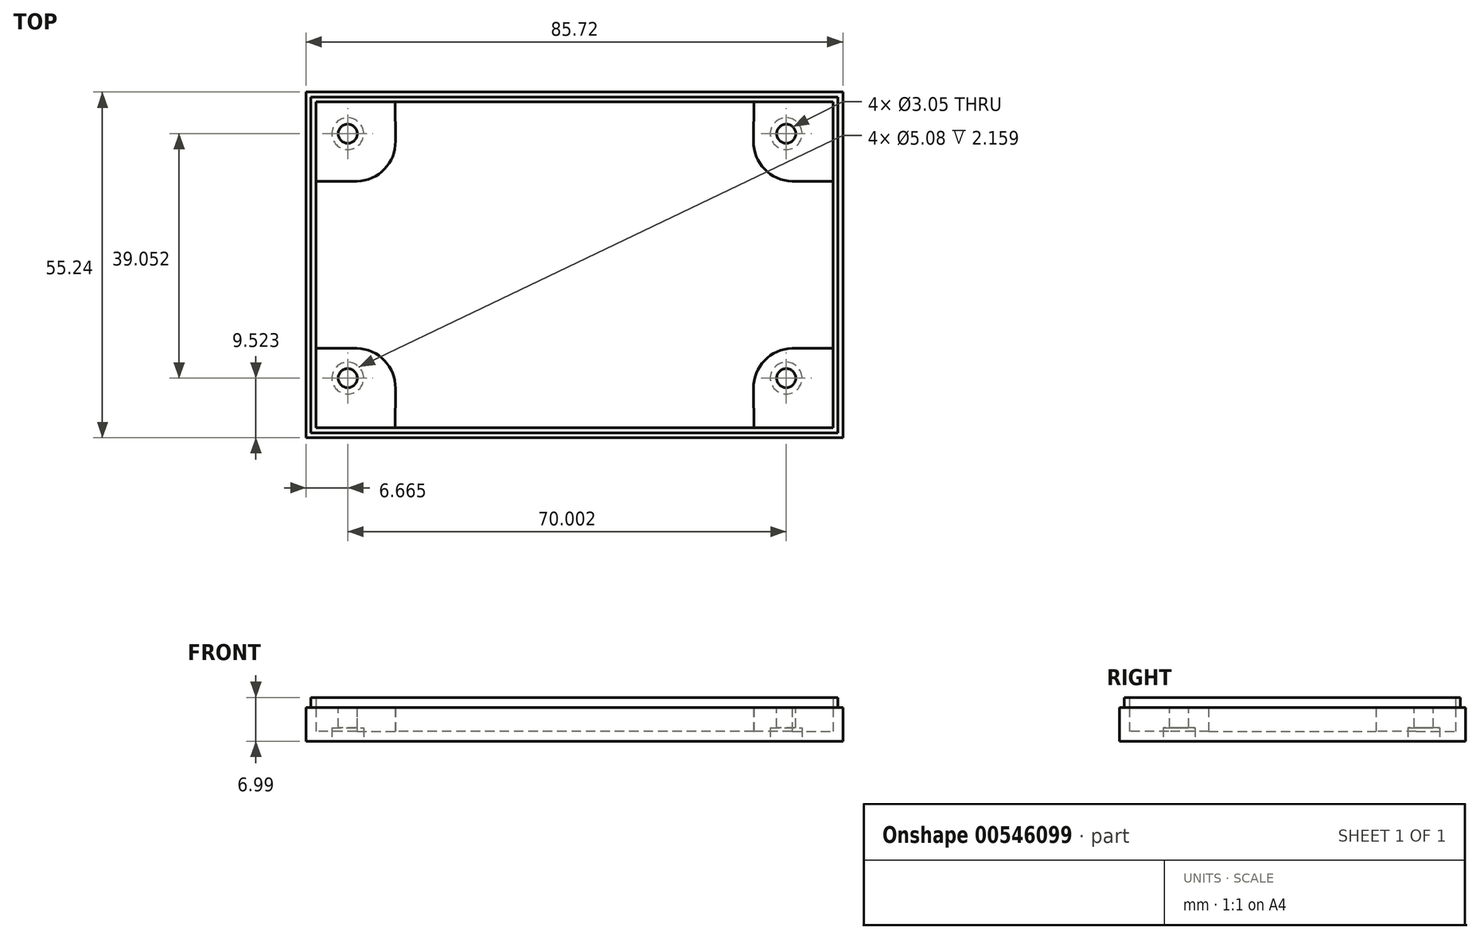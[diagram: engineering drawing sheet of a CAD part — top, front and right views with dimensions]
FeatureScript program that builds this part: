
annotation { "Feature Type Name" : "Feature", "Feature Type Description" : "" }
export const myFeature = defineFeature(function(context is Context, id is Id, definition is map)
    precondition{}
    {
        {
            var Q0;
            Q0=qCreatedBy(makeId("Top.planeOp"),FACE);
            var sketch = newSketch(context, id + "F0", { "sketchPlane" : qUnion([Q0])});
            skLineSegment(sketch, "E0.bottom", {"start": v(42.86, -27.62) * mm, "end": v(-42.86, -27.62) * mm});
            skLineSegment(sketch, "E0.top", {"start": v(42.86, 27.62) * mm, "end": v(-42.86, 27.62) * mm});
            skLineSegment(sketch, "E0.left", {"start": v(42.86, -27.62) * mm, "end": v(42.86, 27.62) * mm});
            skLineSegment(sketch, "E0.right", {"start": v(-42.86, -27.62) * mm, "end": v(-42.86, 27.62) * mm});
            skPoint(sketch, "E0.middle", {"position": v(0, 0) * mm});
            skSolve(sketch);
        }
        {
            var Q0;
            Q0=makeQuery(id+"F0.imprint","IMPRINT",FACE,{"disambiguationData":[TD([[makeQuery(id+"F0.imprint","IMPRINT",EDGE,{"derivedFrom":sQuery(id+"F0.wireOp",EDGE,"E0.bottom")}),-1.0]])]});
            extrude(context, id + "F1", {"entities" : qUnion([Q0]), "depth" : 7 * mm, "offsetDistance" : 25.4 * mm});
        }
        {
            var Q0;
            Q0=makeQuery(id+"F1.opExtrude","CAP_FACE",FACE,{"disambiguationData":[OSD([sQuery(id+"F0.wireOp",EDGE,"E0.bottom"),sQuery(id+"F0.wireOp",EDGE,"E0.top"),sQuery(id+"F0.wireOp",EDGE,"E0.left"),sQuery(id+"F0.wireOp",EDGE,"E0.right")])],"isStart":false});
            shell(context, id + "F2", {"entities" : qUnion([Q0]), "thickness" : 1.59 * mm});
        }
        {
            var Q0;
            Q0=makeQuery(id+"F2.opShell","OFFSET_FACE",FACE,{"disambiguationData":[OSD([sQuery(id+"F0.wireOp",EDGE,"E0.bottom"),sQuery(id+"F0.wireOp",EDGE,"E0.top"),sQuery(id+"F0.wireOp",EDGE,"E0.left"),sQuery(id+"F0.wireOp",EDGE,"E0.right")])]});
            var sketch = newSketch(context, id + "F3", { "sketchPlane" : qUnion([Q0])});
            skArc(sketch, "E1", {"start": v(-35.12, 13.34) * mm, "mid": v(-30.48, 15.15) * mm, "end": v(-28.58, 19.75) * mm});
            skLineSegment(sketch, "E2", {"start": v(-28.58, 19.75) * mm, "end": v(-28.64, 26.04) * mm});
            skLineSegment(sketch, "E3", {"start": v(-34.73, 13.34) * mm, "end": v(-41.28, 13.34) * mm});
            skLineSegment(sketch, "E4.MirrorCS", {"start": v(28.58, 19.75) * mm, "end": v(28.64, 26.04) * mm});
            skArc(sketch, "E5.MirrorCS", {"start": v(35.12, 13.34) * mm, "mid": v(30.48, 15.15) * mm, "end": v(28.58, 19.75) * mm});
            skLineSegment(sketch, "E6.MirrorCS", {"start": v(34.73, 13.34) * mm, "end": v(41.28, 13.34) * mm});
            skLineSegment(sketch, "E7.MirrorCS", {"start": v(-34.73, -13.34) * mm, "end": v(-41.28, -13.34) * mm});
            skArc(sketch, "E8.MirrorCS", {"start": v(-35.12, -13.34) * mm, "mid": v(-30.48, -15.15) * mm, "end": v(-28.58, -19.75) * mm});
            skLineSegment(sketch, "E9.MirrorCS", {"start": v(-28.58, -19.75) * mm, "end": v(-28.64, -26.04) * mm});
            skArc(sketch, "E10.MirrorCS", {"start": v(35.12, -13.34) * mm, "mid": v(30.48, -15.15) * mm, "end": v(28.58, -19.75) * mm});
            skLineSegment(sketch, "E11.MirrorCS", {"start": v(28.58, -19.75) * mm, "end": v(28.64, -26.04) * mm});
            skLineSegment(sketch, "E12.MirrorCS", {"start": v(34.73, -13.34) * mm, "end": v(41.28, -13.34) * mm});
            skSolve(sketch);
        }
        {
            var Q0;
            {var subQ7=sQuery(id+"F3.wireOp",EDGE,"E2");Q0=makeQuery(id+"F3.imprint","IMPRINT",FACE,{"disambiguationData":[TD([[makeQuery(id+"F3.imprint","IMPRINT",EDGE,{"derivedFrom":subQ7}),1.0]])]});}
            var Q1;
            {var subQ7=sQuery(id+"F3.wireOp",EDGE,"E4.MirrorCS");Q1=makeQuery(id+"F3.imprint","IMPRINT",FACE,{"disambiguationData":[TD([[makeQuery(id+"F3.imprint","IMPRINT",EDGE,{"derivedFrom":subQ7}),-1.0]])]});}
            var Q2;
            {var subQ7=sQuery(id+"F3.wireOp",EDGE,"E11.MirrorCS");Q2=makeQuery(id+"F3.imprint","IMPRINT",FACE,{"disambiguationData":[TD([[makeQuery(id+"F3.imprint","IMPRINT",EDGE,{"derivedFrom":subQ7}),1.0]])]});}
            var Q3;
            {var subQ0=sQuery(id+"F3.wireOp",EDGE,"E9.MirrorCS");Q3=makeQuery(id+"F3.imprint","IMPRINT",FACE,{"disambiguationData":[TD([[makeQuery(id+"F3.imprint","IMPRINT",EDGE,{"derivedFrom":subQ0}),-1.0]])]});}
            extrude(context, id + "F4", {"entities" : qUnion([Q0, Q1, Q2, Q3]), "operationType" : NewBodyOperationType.ADD, "depth" : 3.77 * mm, "offsetDistance" : 25.4 * mm});
        }
        {
            var Q0;
            Q0=makeQuery(id+"F4.opExtrude","CAP_FACE",FACE,{"disambiguationData":[OSD([sQuery(id+"F0.wireOp",EDGE,"E0.top"),sQuery(id+"F0.wireOp",EDGE,"E0.right"),sQuery(id+"F3.wireOp",EDGE,"E1"),sQuery(id+"F3.wireOp",EDGE,"E2"),sQuery(id+"F3.wireOp",EDGE,"E3")])],"isStart":false});
            var sketch = newSketch(context, id + "F5", { "sketchPlane" : qUnion([Q0])});
            skCircle(sketch, "E13", {"center": v(-36.2, 20.95) * mm, "radius": 1.52 * mm});
            skLineSegment(sketch, "E14.bottom", {"start": v(-36.2, 20.95) * mm, "end": v(33.8, 20.95) * mm, "construction": true});
            skLineSegment(sketch, "E14.top", {"start": v(-36.2, -18.1) * mm, "end": v(33.8, -18.1) * mm, "construction": true});
            skLineSegment(sketch, "E14.left", {"start": v(-36.2, 20.96) * mm, "end": v(-36.2, -18.1) * mm, "construction": true});
            skLineSegment(sketch, "E14.right", {"start": v(33.8, 20.96) * mm, "end": v(33.8, -18.1) * mm, "construction": true});
            skCircle(sketch, "E15", {"center": v(-36.2, -18.1) * mm, "radius": 1.52 * mm});
            skCircle(sketch, "E16", {"center": v(33.8, 20.95) * mm, "radius": 1.52 * mm});
            skCircle(sketch, "E17", {"center": v(33.8, -18.1) * mm, "radius": 1.52 * mm});
            skSolve(sketch);
        }
        {
            var Q0;
            Q0=makeQuery(id+"F5.imprint","IMPRINT",FACE,{"disambiguationData":[TD([[makeQuery(id+"F5.imprint","IMPRINT",EDGE,{"derivedFrom":sQuery(id+"F5.wireOp",EDGE,"E16")}),1.0]])]});
            var Q1;
            Q1=makeQuery(id+"F5.imprint","IMPRINT",FACE,{"disambiguationData":[TD([[makeQuery(id+"F5.imprint","IMPRINT",EDGE,{"derivedFrom":sQuery(id+"F5.wireOp",EDGE,"E13")}),1.0]])]});
            var Q2;
            Q2=makeQuery(id+"F5.imprint","IMPRINT",FACE,{"disambiguationData":[TD([[makeQuery(id+"F5.imprint","IMPRINT",EDGE,{"derivedFrom":sQuery(id+"F5.wireOp",EDGE,"E15")}),1.0]])]});
            var Q3;
            Q3=makeQuery(id+"F5.imprint","IMPRINT",FACE,{"disambiguationData":[TD([[makeQuery(id+"F5.imprint","IMPRINT",EDGE,{"derivedFrom":sQuery(id+"F5.wireOp",EDGE,"E17")}),1.0]])]});
            extrude(context, id + "F6", {"entities" : qUnion([Q0, Q1, Q2, Q3]), "operationType" : NewBodyOperationType.REMOVE, "endBound" : BoundingType.THROUGH_ALL, "oppositeDirection" : true, "depth" : 25.4 * mm, "offsetDistance" : 25.4 * mm});
        }
        {
            var Q0;
            Q0=makeQuery(id+"F1.opExtrude","CAP_FACE",FACE,{"disambiguationData":[OSD([sQuery(id+"F0.wireOp",EDGE,"E0.bottom"),sQuery(id+"F0.wireOp",EDGE,"E0.top"),sQuery(id+"F0.wireOp",EDGE,"E0.left"),sQuery(id+"F0.wireOp",EDGE,"E0.right")])],"isStart":true});
            var sketch = newSketch(context, id + "F7", { "sketchPlane" : qUnion([Q0])});
            skCircle(sketch, "E18", {"center": v(33.8, 18.1) * mm, "radius": 2.54 * mm});
            skCircle(sketch, "E19", {"center": v(33.8, -20.95) * mm, "radius": 2.54 * mm});
            skCircle(sketch, "E20", {"center": v(-36.2, -20.95) * mm, "radius": 2.54 * mm});
            skCircle(sketch, "E21", {"center": v(-36.2, 18.1) * mm, "radius": 2.54 * mm});
            skSolve(sketch);
        }
        {
            var Q0;
            Q0=makeQuery(id+"F7.imprint","IMPRINT",FACE,{"disambiguationData":[TD([[makeQuery(id+"F7.imprint","IMPRINT",EDGE,{"derivedFrom":sQuery(id+"F7.wireOp",EDGE,"E21")}),1.0]])]});
            var Q1;
            Q1=makeQuery(id+"F7.imprint","IMPRINT",FACE,{"disambiguationData":[TD([[makeQuery(id+"F7.imprint","IMPRINT",EDGE,{"derivedFrom":sQuery(id+"F7.wireOp",EDGE,"E18")}),1.0]])]});
            var Q2;
            Q2=makeQuery(id+"F7.imprint","IMPRINT",FACE,{"disambiguationData":[TD([[makeQuery(id+"F7.imprint","IMPRINT",EDGE,{"derivedFrom":sQuery(id+"F7.wireOp",EDGE,"E19")}),1.0]])]});
            var Q3;
            Q3=makeQuery(id+"F7.imprint","IMPRINT",FACE,{"disambiguationData":[TD([[makeQuery(id+"F7.imprint","IMPRINT",EDGE,{"derivedFrom":sQuery(id+"F7.wireOp",EDGE,"E20")}),1.0]])]});
            extrude(context, id + "F8", {"entities" : qUnion([Q0, Q1, Q2, Q3]), "operationType" : NewBodyOperationType.REMOVE, "oppositeDirection" : true, "depth" : 2.16 * mm, "offsetDistance" : 25.4 * mm});
        }
        {
            var Q0;
            Q0=makeQuery(id+"F1.opExtrude","CAP_FACE",FACE,{"disambiguationData":[OSD([sQuery(id+"F0.wireOp",EDGE,"E0.bottom"),sQuery(id+"F0.wireOp",EDGE,"E0.top"),sQuery(id+"F0.wireOp",EDGE,"E0.left"),sQuery(id+"F0.wireOp",EDGE,"E0.right")])],"isStart":false});
            var sketch = newSketch(context, id + "F9", { "sketchPlane" : qUnion([Q0])});
            skLineSegment(sketch, "E22", {"start": v(-42.86, -27.62) * mm, "end": v(-41.27, -26.04) * mm, "construction": true});
            skLineSegment(sketch, "E23", {"start": v(41.28, 26.04) * mm, "end": v(42.86, 27.62) * mm, "construction": true});
            skLineSegment(sketch, "E24.bottom", {"start": v(-42.07, -26.83) * mm, "end": v(42.07, -26.83) * mm});
            skLineSegment(sketch, "E24.top", {"start": v(-42.07, 26.83) * mm, "end": v(42.07, 26.83) * mm});
            skLineSegment(sketch, "E24.left", {"start": v(-42.07, -26.83) * mm, "end": v(-42.07, 26.83) * mm});
            skLineSegment(sketch, "E24.right", {"start": v(42.07, -26.83) * mm, "end": v(42.07, 26.83) * mm});
            skSolve(sketch);
        }
        {
            var Q0;
            Q0=makeQuery(id+"F9.imprint","IMPRINT",FACE,{"disambiguationData":[TD([[makeQuery(id+"F9.imprint","IMPRINT",EDGE,{"derivedFrom":sQuery(id+"F9.wireOp",EDGE,"E24.bottom")}),-1.0]])]});
            extrude(context, id + "F10", {"entities" : qUnion([Q0]), "operationType" : NewBodyOperationType.REMOVE, "oppositeDirection" : true, "depth" : 1.63 * mm, "offsetDistance" : 25.4 * mm});
        }
    });
